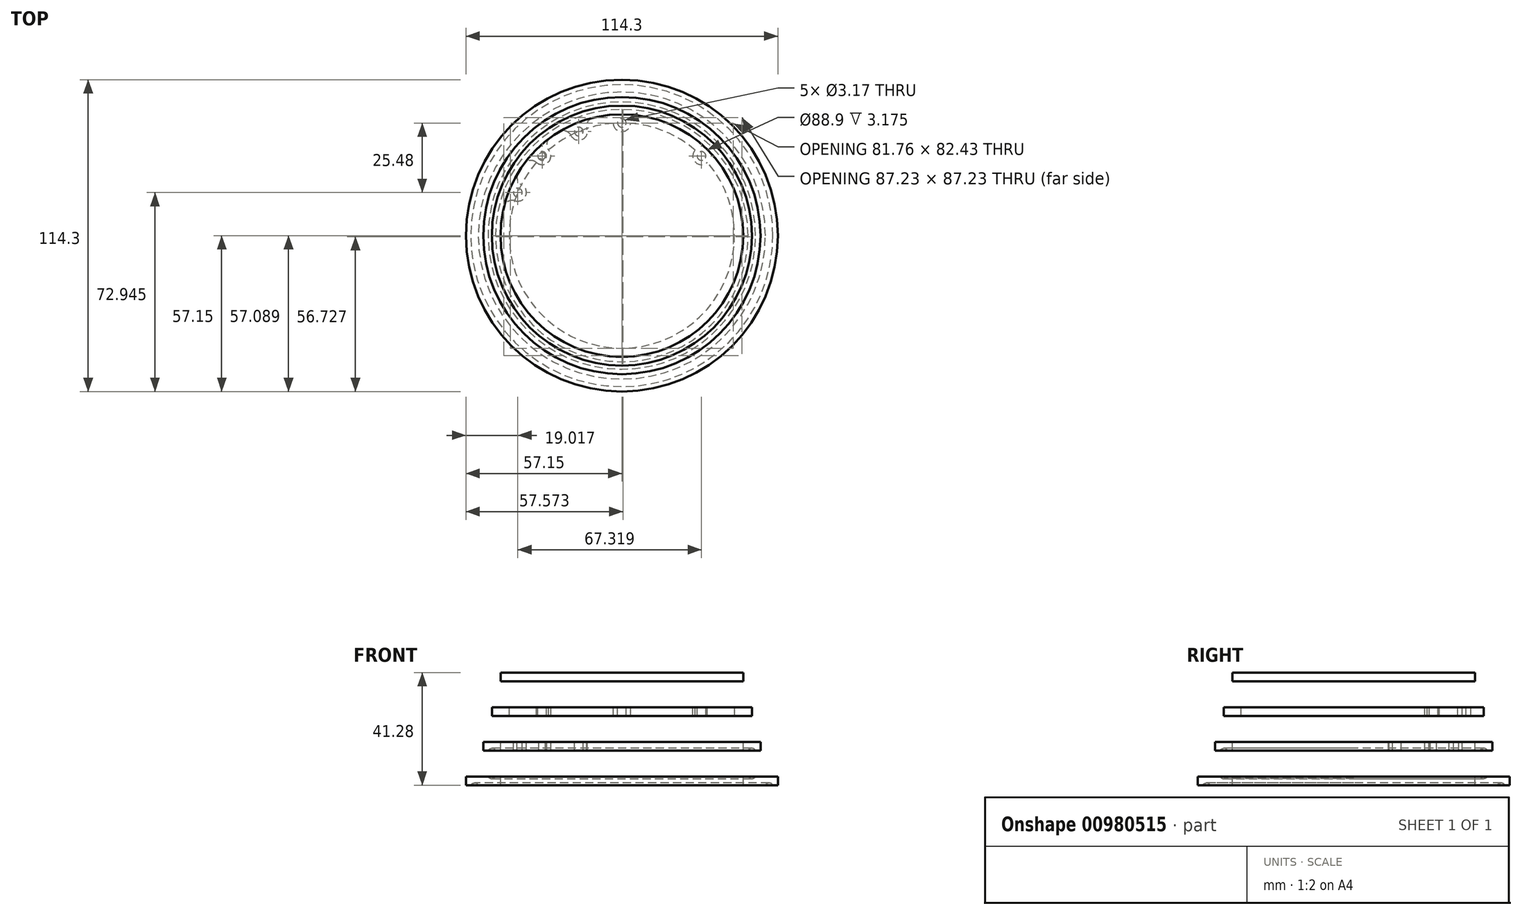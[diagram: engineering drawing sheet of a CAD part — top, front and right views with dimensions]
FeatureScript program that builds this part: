
annotation { "Feature Type Name" : "Feature", "Feature Type Description" : "" }
export const myFeature = defineFeature(function(context is Context, id is Id, definition is map)
    precondition{}
    {
        {
            var Q0;
            Q0=qCreatedBy(makeId("Front.planeOp"),FACE);
            var sketch = newSketch(context, id + "F0", { "sketchPlane" : qUnion([Q0])});
            skLineSegment(sketch, "E0.bottom", {"start": v(-44.45, 0) * mm, "end": v(-52.6, 0) * mm});
            skLineSegment(sketch, "E0.left", {"start": v(-44.45, 0) * mm, "end": v(-44.45, 3.17) * mm});
            skLineSegment(sketch, "E0.right", {"start": v(-57.15, 0) * mm, "end": v(-57.15, 3.17) * mm});
            skArc(sketch, "E1", {"start": v(-52.6, 0) * mm, "mid": v(-53.98, 0.8) * mm, "end": v(-55.35, 0) * mm});
            skArc(sketch, "E2", {"start": v(-49, 3.17) * mm, "mid": v(-47.62, 2.38) * mm, "end": v(-46.25, 3.17) * mm});
            skLineSegment(sketch, "E3", {"start": v(-57.15, 3.17) * mm, "end": v(-49, 3.17) * mm});
            skLineSegment(sketch, "E4", {"start": v(-49, 3.17) * mm, "end": v(-46.25, 3.17) * mm, "construction": true});
            skLineSegment(sketch, "E5", {"start": v(-46.25, 3.17) * mm, "end": v(-44.45, 3.17) * mm});
            skLineSegment(sketch, "E6", {"start": v(-55.35, 0) * mm, "end": v(-57.15, 0) * mm});
            skLineSegment(sketch, "E7", {"start": v(-52.6, 0) * mm, "end": v(-55.35, 0) * mm, "construction": true});
            skLineSegment(sketch, "E8", {"start": v(0, 3.17) * mm, "end": v(0, 0) * mm, "construction": true});
            skLineSegment(sketch, "E9.bottom", {"start": v(-44.45, 12.7) * mm, "end": v(-46.25, 12.7) * mm});
            skLineSegment(sketch, "E9.top", {"start": v(-44.45, 15.87) * mm, "end": v(-50.8, 15.87) * mm});
            skLineSegment(sketch, "E9.left", {"start": v(-44.45, 12.7) * mm, "end": v(-44.45, 15.87) * mm});
            skLineSegment(sketch, "E9.right", {"start": v(-50.8, 12.7) * mm, "end": v(-50.8, 15.87) * mm});
            skArc(sketch, "E10", {"start": v(-46.25, 12.7) * mm, "mid": v(-47.62, 13.5) * mm, "end": v(-49, 12.7) * mm});
            skLineSegment(sketch, "E11", {"start": v(-49, 12.7) * mm, "end": v(-50.8, 12.7) * mm});
            skLineSegment(sketch, "E12", {"start": v(-46.25, 12.7) * mm, "end": v(-49, 12.7) * mm, "construction": true});
            skLineSegment(sketch, "E13.bottom", {"start": v(-44.45, 41.27) * mm, "end": v(0, 41.27) * mm});
            skLineSegment(sketch, "E13.top", {"start": v(-44.45, 38.1) * mm, "end": v(0, 38.1) * mm});
            skLineSegment(sketch, "E13.left", {"start": v(-44.45, 41.27) * mm, "end": v(-44.45, 38.1) * mm});
            skLineSegment(sketch, "E13.right", {"start": v(0, 41.27) * mm, "end": v(0, 38.1) * mm});
            skLineSegment(sketch, "E14.bottom", {"start": v(-47.62, 28.57) * mm, "end": v(-41.27, 28.57) * mm});
            skLineSegment(sketch, "E14.top", {"start": v(-47.62, 25.4) * mm, "end": v(-41.27, 25.4) * mm});
            skLineSegment(sketch, "E14.left", {"start": v(-47.62, 28.57) * mm, "end": v(-47.62, 25.4) * mm});
            skLineSegment(sketch, "E14.right", {"start": v(-41.27, 28.57) * mm, "end": v(-41.27, 25.4) * mm});
            skSolve(sketch);
        }
        {
            var Q0;
            Q0=makeQuery(id+"F0.imprint","IMPRINT",FACE,{"disambiguationData":[TD([[makeQuery(id+"F0.imprint","IMPRINT",EDGE,{"derivedFrom":sQuery(id+"F0.wireOp",EDGE,"E0.bottom")}),-1.0]])]});
            var Q1;
            Q1=makeQuery(id+"F0.imprint","IMPRINT",FACE,{"disambiguationData":[TD([[makeQuery(id+"F0.imprint","IMPRINT",EDGE,{"derivedFrom":sQuery(id+"F0.wireOp",EDGE,"E9.bottom")}),-1.0]])]});
            var Q2;
            Q2=makeQuery(id+"F0.imprint","IMPRINT",FACE,{"disambiguationData":[TD([[makeQuery(id+"F0.imprint","IMPRINT",EDGE,{"derivedFrom":sQuery(id+"F0.wireOp",EDGE,"E13.bottom")}),-1.0]])]});
            var Q3;
            Q3=makeQuery(id+"F0.imprint","IMPRINT",FACE,{"disambiguationData":[TD([[makeQuery(id+"F0.imprint","IMPRINT",EDGE,{"derivedFrom":sQuery(id+"F0.wireOp",EDGE,"E14.bottom")}),-1.0]])]});
            var Q4;
            Q4=sQuery(id+"F0.wireOp",EDGE,"E8");
            revolve(context, id + "F1", {"surfaceOperationType" : NewSurfaceOperationType.NEW, "entities" : qUnion([Q0, Q1, Q2, Q3]), "axis" : qUnion([Q4]), "revolveType" : RevolveType.FULL});
        }
        {
            var Q0;
            Q0=qCreatedBy(makeId("Top.planeOp"),FACE);
            var sketch = newSketch(context, id + "F2", { "sketchPlane" : qUnion([Q0])});
            skCircle(sketch, "E15", {"center": v(0, 0) * mm, "radius": 44.45 * mm, "construction": true});
            skCircle(sketch, "E16", {"center": v(0, 0) * mm, "radius": 41.28 * mm, "construction": true});
            skPoint(sketch, "E17", {"position": v(-41.28, 0) * mm});
            skPoint(sketch, "E18.1.0", {"position": v(-38.13, -15.8) * mm});
            skPoint(sketch, "E18.2.0", {"position": v(-29.19, -29.19) * mm});
            skPoint(sketch, "E18.3.0", {"position": v(-15.8, -38.13) * mm});
            skPoint(sketch, "E18.4.0", {"position": v(0, -41.27) * mm});
            skPoint(sketch, "E18.5.0", {"position": v(15.8, -38.13) * mm});
            skPoint(sketch, "E18.6.0", {"position": v(29.19, -29.19) * mm});
            skPoint(sketch, "E18.7.0", {"position": v(38.13, -15.8) * mm});
            skPoint(sketch, "E18.8.0", {"position": v(41.27, 0) * mm});
            skPoint(sketch, "E18.9.0", {"position": v(38.13, 15.8) * mm});
            skPoint(sketch, "E18.10.0", {"position": v(29.19, 29.19) * mm});
            skPoint(sketch, "E18.11.0", {"position": v(15.8, 38.13) * mm});
            skPoint(sketch, "E19.0.12.0", {"position": v(0, 41.28) * mm});
            skPoint(sketch, "E19.0.13.0", {"position": v(-15.8, 38.13) * mm});
            skPoint(sketch, "E19.0.14.0", {"position": v(-29.19, 29.19) * mm});
            skPoint(sketch, "E19.0.15.0", {"position": v(-38.13, 15.8) * mm});
            skSolve(sketch);
        }
        {
            var Q0;
            Q0=makeQuery(id+"F1.opRevolve","SWEPT_FACE",FACE,{"disambiguationData":[OSD([sQuery(id+"F0.wireOp",EDGE,"E9.top")])]});
            var sketch = newSketch(context, id + "F3", { "sketchPlane" : qUnion([Q0])});
            skCircle(sketch, "E20", {"center": v(-38.13, 15.8) * mm, "radius": 1.59 * mm});
            skCircle(sketch, "E21", {"center": v(-15.8, 38.13) * mm, "radius": 1.59 * mm});
            skArc(sketch, "E22", {"start": v(-39.12, 12.78) * mm, "mid": v(-35.2, 14.58) * mm, "end": v(-36.7, 18.63) * mm});
            skArc(sketch, "E23", {"start": v(-18.63, 36.7) * mm, "mid": v(-14.58, 35.2) * mm, "end": v(-12.78, 39.12) * mm});
            skArc(sketch, "E24", {"start": v(-43.19, 10.5) * mm, "mid": v(31.43, -31.43) * mm, "end": v(-10.5, 43.19) * mm, "construction": true});
            skArc(sketch, "E25", {"start": v(-37.97, 23.1) * mm, "mid": v(-41.07, 17.01) * mm, "end": v(-43.19, 10.5) * mm});
            skArc(sketch, "E26", {"start": v(-23.1, 37.97) * mm, "mid": v(-31.43, 31.43) * mm, "end": v(-37.97, 23.1) * mm, "construction": true});
            skArc(sketch, "E27", {"start": v(-10.5, 43.19) * mm, "mid": v(-17.01, 41.07) * mm, "end": v(-23.1, 37.97) * mm});
            skPoint(sketch, "E28.visualSharp", {"position": v(-41.07, 17.01) * mm});
            skArc(sketch, "E28.filletArc", {"start": v(-39.12, 12.78) * mm, "mid": v(-41.65, 12.53) * mm, "end": v(-43.19, 10.5) * mm});
            skArc(sketch, "E29.filletArc", {"start": v(-37.97, 23.1) * mm, "mid": v(-38.31, 20.59) * mm, "end": v(-36.7, 18.63) * mm});
            skPoint(sketch, "E30.visualSharp", {"position": v(-17.01, 41.07) * mm});
            skArc(sketch, "E30.filletArc", {"start": v(-18.63, 36.7) * mm, "mid": v(-20.59, 38.31) * mm, "end": v(-23.1, 37.97) * mm});
            skArc(sketch, "E31.filletArc", {"start": v(-10.5, 43.19) * mm, "mid": v(-12.53, 41.65) * mm, "end": v(-12.78, 39.12) * mm});
            skCircle(sketch, "E32", {"center": v(-41.28, 0) * mm, "radius": 1.2 * mm});
            skCircle(sketch, "E33", {"center": v(-29.19, 29.19) * mm, "radius": 1.2 * mm});
            skArc(sketch, "E34", {"start": v(-41.03, -3.17) * mm, "mid": v(-38.1, 0) * mm, "end": v(-41.03, 3.17) * mm});
            skArc(sketch, "E35", {"start": v(-31.25, 26.77) * mm, "mid": v(-26.94, 26.94) * mm, "end": v(-26.77, 31.25) * mm});
            skArc(sketch, "E36", {"start": v(-43.92, 6.82) * mm, "mid": v(-43.28, 4.36) * mm, "end": v(-41.03, 3.17) * mm});
            skArc(sketch, "E37", {"start": v(-41.03, -3.17) * mm, "mid": v(-43.28, -4.36) * mm, "end": v(-43.92, -6.82) * mm});
            skArc(sketch, "E38", {"start": v(-31.25, 26.77) * mm, "mid": v(-33.68, 27.52) * mm, "end": v(-35.88, 26.24) * mm});
            skArc(sketch, "E39", {"start": v(-26.24, 35.88) * mm, "mid": v(-27.52, 33.68) * mm, "end": v(-26.77, 31.25) * mm});
            skSolve(sketch);
        }
        {
            var Q0;
            Q0=makeQuery(id+"F3.imprint","IMPRINT",FACE,{"disambiguationData":[TD([[makeQuery(id+"F3.imprint","IMPRINT",EDGE,{"derivedFrom":sQuery(id+"F3.wireOp",EDGE,"E20")}),-1.0]])]});
            var Q1;
            Q1=makeQuery(id+"F3.imprint","IMPRINT",FACE,{"disambiguationData":[TD([[makeQuery(id+"F3.imprint","IMPRINT",EDGE,{"derivedFrom":sQuery(id+"F3.wireOp",EDGE,"E21")}),-1.0]])]});
            var Q2;
            Q2=makeQuery(id+"F3.imprint","IMPRINT",FACE,{"disambiguationData":[TD([[makeQuery(id+"F3.imprint","IMPRINT",EDGE,{"derivedFrom":sQuery(id+"F3.wireOp",EDGE,"E33")}),-1.0]])]});
            var Q3;
            Q3=makeQuery(id+"F3.imprint","IMPRINT",FACE,{"disambiguationData":[TD([[makeQuery(id+"F3.imprint","IMPRINT",EDGE,{"derivedFrom":sQuery(id+"F3.wireOp",EDGE,"E32")}),-1.0]])]});
            var Q4;
            Q4=makeQuery(id+"F1.opRevolve","SWEPT_FACE",FACE,{"disambiguationData":[OSD([sQuery(id+"F0.wireOp",EDGE,"E9.bottom")])]});
            extrude(context, id + "F4", {"entities" : qUnion([Q0, Q1, Q2, Q3]), "operationType" : NewBodyOperationType.ADD, "endBound" : BoundingType.UP_TO_SURFACE, "oppositeDirection" : true, "depth" : 25.4 * mm, "endBoundEntityFace" : qUnion([Q4]), "offsetDistance" : 25.4 * mm});
        }
        {
            var Q0;
            {var subQ0=sQuery(id+"F3.wireOp",EDGE,"E39");var subQ1=sQuery(id+"F3.wireOp",EDGE,"E38");var subQ2=sQuery(id+"F3.wireOp",EDGE,"E35");var subQ3=sQuery(id+"F3.wireOp",EDGE,"E33");var subQ4=sQuery(id+"F0.wireOp",EDGE,"E9.left");var subQ5=sQuery(id+"F0.wireOp",EDGE,"E9.top");var subQ6=sQuery(id+"F3.wireOp",EDGE,"E37");var subQ7=sQuery(id+"F3.wireOp",EDGE,"E36");var subQ8=sQuery(id+"F3.wireOp",EDGE,"E34");var subQ9=sQuery(id+"F3.wireOp",EDGE,"E32");var subQ10=sQuery(id+"F3.wireOp",EDGE,"E31.filletArc");var subQ11=sQuery(id+"F3.wireOp",EDGE,"E30.filletArc");var subQ12=sQuery(id+"F3.wireOp",EDGE,"E27");var subQ13=sQuery(id+"F3.wireOp",EDGE,"E23");var subQ14=sQuery(id+"F3.wireOp",EDGE,"E21");var subQ15=sQuery(id+"F3.wireOp",EDGE,"E29.filletArc");var subQ16=sQuery(id+"F3.wireOp",EDGE,"E28.filletArc");var subQ17=sQuery(id+"F3.wireOp",EDGE,"E25");var subQ18=sQuery(id+"F3.wireOp",EDGE,"E22");var subQ19=sQuery(id+"F3.wireOp",EDGE,"E20");Q0=makeQuery(id+"FB8sXTdEjQkzu1t_4.3.F4.boolean.opBoolean","MERGE",FACE,{"derivedFrom":[makeQuery(id+"FB8sXTdEjQkzu1t_4.2.F4.boolean.opBoolean","MERGE",FACE,{"derivedFrom":[makeQuery(id+"FB8sXTdEjQkzu1t_4.1.F4.boolean.opBoolean","MERGE",FACE,{"derivedFrom":[makeQuery(id+"F4.boolean.opBoolean","MERGE",FACE,{"derivedFrom":[makeQuery(id+"F1.opRevolve","SWEPT_FACE",FACE,{"disambiguationData":[OSD([subQ5])]}),makeQuery(id+"F4.opExtrude","CAP_FACE",FACE,{"disambiguationData":[OSD([subQ19,subQ18,subQ17,subQ16,subQ15])],"isStart":true}),makeQuery(id+"F4.opExtrude","CAP_FACE",FACE,{"disambiguationData":[OSD([subQ14,subQ13,subQ12,subQ11,subQ10])],"isStart":true}),makeQuery(id+"F4.opExtrude","CAP_FACE",FACE,{"disambiguationData":[OSD([subQ5,subQ4,subQ9,subQ8,subQ7,subQ6])],"isStart":true}),makeQuery(id+"F4.opExtrude","CAP_FACE",FACE,{"disambiguationData":[OSD([subQ5,subQ4,subQ3,subQ2,subQ1,subQ0])],"isStart":true})]}),makeQuery(id+"FB8sXTdEjQkzu1t_4.1.F4.opExtrude","CAP_FACE",FACE,{"disambiguationData":[OSD([subQ19,subQ18,subQ17,subQ16,subQ15])],"isStart":true}),makeQuery(id+"FB8sXTdEjQkzu1t_4.1.F4.opExtrude","CAP_FACE",FACE,{"disambiguationData":[OSD([subQ14,subQ13,subQ12,subQ11,subQ10])],"isStart":true}),makeQuery(id+"FB8sXTdEjQkzu1t_4.1.F4.opExtrude","CAP_FACE",FACE,{"disambiguationData":[OSD([subQ5,subQ4,subQ9,subQ8,subQ7,subQ6])],"isStart":true}),makeQuery(id+"FB8sXTdEjQkzu1t_4.1.F4.opExtrude","CAP_FACE",FACE,{"disambiguationData":[OSD([subQ5,subQ4,subQ3,subQ2,subQ1,subQ0])],"isStart":true})]}),makeQuery(id+"FB8sXTdEjQkzu1t_4.2.F4.opExtrude","CAP_FACE",FACE,{"disambiguationData":[OSD([subQ19,subQ18,subQ17,subQ16,subQ15])],"isStart":true}),makeQuery(id+"FB8sXTdEjQkzu1t_4.2.F4.opExtrude","CAP_FACE",FACE,{"disambiguationData":[OSD([subQ14,subQ13,subQ12,subQ11,subQ10])],"isStart":true}),makeQuery(id+"FB8sXTdEjQkzu1t_4.2.F4.opExtrude","CAP_FACE",FACE,{"disambiguationData":[OSD([subQ5,subQ4,subQ9,subQ8,subQ7,subQ6])],"isStart":true}),makeQuery(id+"FB8sXTdEjQkzu1t_4.2.F4.opExtrude","CAP_FACE",FACE,{"disambiguationData":[OSD([subQ5,subQ4,subQ3,subQ2,subQ1,subQ0])],"isStart":true})]}),makeQuery(id+"FB8sXTdEjQkzu1t_4.3.F4.opExtrude","CAP_FACE",FACE,{"disambiguationData":[OSD([subQ19,subQ18,subQ17,subQ16,subQ15])],"isStart":true}),makeQuery(id+"FB8sXTdEjQkzu1t_4.3.F4.opExtrude","CAP_FACE",FACE,{"disambiguationData":[OSD([subQ14,subQ13,subQ12,subQ11,subQ10])],"isStart":true}),makeQuery(id+"FB8sXTdEjQkzu1t_4.3.F4.opExtrude","CAP_FACE",FACE,{"disambiguationData":[OSD([subQ5,subQ4,subQ9,subQ8,subQ7,subQ6])],"isStart":true}),makeQuery(id+"FB8sXTdEjQkzu1t_4.3.F4.opExtrude","CAP_FACE",FACE,{"disambiguationData":[OSD([subQ5,subQ4,subQ3,subQ2,subQ1,subQ0])],"isStart":true})]});}
            var sketch = newSketch(context, id + "F5", { "sketchPlane" : qUnion([Q0])});
            skArc(sketch, "E40", {"start": v(-43.19, 10.5) * mm, "mid": v(-44.45, 0) * mm, "end": v(-43.19, -10.5) * mm});
            skLineSegment(sketch, "E41", {"start": v(-43.19, 10.5) * mm, "end": v(43.19, 10.5) * mm});
            skLineSegment(sketch, "E42", {"start": v(43.19, -10.5) * mm, "end": v(-43.19, -10.5) * mm});
            skArc(sketch, "E43.trimOffspring", {"start": v(43.19, -10.5) * mm, "mid": v(44.45, 0) * mm, "end": v(43.19, 10.5) * mm});
            skSolve(sketch);
        }
        {
            var Q0;
            Q0=makeQuery(id+"F5.imprint","IMPRINT",FACE,{"disambiguationData":[TD([[makeQuery(id+"F5.imprint","IMPRINT",EDGE,{"derivedFrom":makeQuery(id+"F4.opExtrude","CAP_EDGE",EDGE,{"disambiguationData":[OSD([sQuery(id+"F3.wireOp",EDGE,"E32")])],"isStart":true})}),-1.0]])]});
            var Q1;
            Q1=makeQuery(id+"F5.imprint","IMPRINT",FACE,{"disambiguationData":[TD([[makeQuery(id+"F5.imprint","IMPRINT",EDGE,{"derivedFrom":makeQuery(id+"FB8sXTdEjQkzu1t_4.2.F4.opExtrude","CAP_EDGE",EDGE,{"disambiguationData":[OSD([sQuery(id+"F3.wireOp",EDGE,"E32")])],"isStart":true})}),-1.0]])]});
            extrude(context, id + "F6", {"entities" : qUnion([Q0, Q1]), "operationType" : NewBodyOperationType.REMOVE, "oppositeDirection" : true, "depth" : 25.4 * mm, "offsetDistance" : 25.4 * mm});
        }
        {
            var Q0;
            Q0=makeQuery(id+"F1.opRevolve","SWEPT_FACE",FACE,{"disambiguationData":[OSD([sQuery(id+"F0.wireOp",EDGE,"E14.bottom")])]});
            var sketch = newSketch(context, id + "F7", { "sketchPlane" : qUnion([Q0])});
            skCircle(sketch, "E44", {"center": v(-29.19, 29.19) * mm, "radius": 1.59 * mm});
            skCircle(sketch, "E45", {"center": v(-29.19, 29.19) * mm, "radius": 3.18 * mm});
            skCircle(sketch, "E46", {"center": v(0, 41.28) * mm, "radius": 3.18 * mm});
            skCircle(sketch, "E47", {"center": v(0, 41.28) * mm, "radius": 1.59 * mm});
            skCircle(sketch, "E48", {"center": v(29.19, 29.19) * mm, "radius": 3.18 * mm});
            skCircle(sketch, "E49", {"center": v(29.19, 29.19) * mm, "radius": 1.59 * mm});
            skSolve(sketch);
        }
        {
            var Q0;
            Q0 = qSketchRegion(id + "F7", true);
            var Q1;
            Q1=makeQuery(id+"F1.opRevolve","SWEPT_FACE",FACE,{"disambiguationData":[OSD([sQuery(id+"F0.wireOp",EDGE,"E14.top")])]});
            extrude(context, id + "F8", {"entities" : qUnion([Q0]), "operationType" : NewBodyOperationType.ADD, "endBound" : BoundingType.UP_TO_SURFACE, "oppositeDirection" : true, "depth" : 25.4 * mm, "endBoundEntityFace" : qUnion([Q1]), "offsetDistance" : 25.4 * mm});
        }
        {
            var Q0;
            {var subQ0=sQuery(id+"F7.wireOp",EDGE,"E44");var subQ1=makeQuery(id+"F1.opRevolve","SWEPT_EDGE",EDGE,{"disambiguationData":[OSD([sQuery(id+"F0.wireOp",EDGE,"E14.bottom"),sQuery(id+"F0.wireOp",EDGE,"E14.right")])]});var subQ2=makeQuery(id+"F7.imprint","INTERSECT",VERTEX,{"disambiguationData":[OD(0.0)],"derivedFrom":[subQ1,subQ0]});Q0=makeQuery(id+"F7.imprint","IMPRINT",FACE,{"disambiguationData":[TD([[makeQuery(id+"F7.imprint","IMPRINT",EDGE,{"disambiguationData":[TD([[subQ2,1.0]])],"derivedFrom":subQ0}),1.0]])]});}
            var Q1;
            {var subQ0=sQuery(id+"F7.wireOp",EDGE,"E47");var subQ1=makeQuery(id+"F1.opRevolve","SWEPT_EDGE",EDGE,{"disambiguationData":[OSD([sQuery(id+"F0.wireOp",EDGE,"E14.bottom"),sQuery(id+"F0.wireOp",EDGE,"E14.right")])]});var subQ2=makeQuery(id+"F7.imprint","INTERSECT",VERTEX,{"disambiguationData":[OD(0.0)],"derivedFrom":[subQ1,subQ0]});Q1=makeQuery(id+"F7.imprint","IMPRINT",FACE,{"disambiguationData":[TD([[makeQuery(id+"F7.imprint","IMPRINT",EDGE,{"disambiguationData":[TD([[subQ2,1.0]])],"derivedFrom":subQ0}),1.0]])]});}
            var Q2;
            {var subQ0=sQuery(id+"F7.wireOp",EDGE,"E49");var subQ1=makeQuery(id+"F1.opRevolve","SWEPT_EDGE",EDGE,{"disambiguationData":[OSD([sQuery(id+"F0.wireOp",EDGE,"E14.bottom"),sQuery(id+"F0.wireOp",EDGE,"E14.right")])]});var subQ2=makeQuery(id+"F7.imprint","INTERSECT",VERTEX,{"disambiguationData":[OD(0.0)],"derivedFrom":[subQ1,subQ0]});Q2=makeQuery(id+"F7.imprint","IMPRINT",FACE,{"disambiguationData":[TD([[makeQuery(id+"F7.imprint","IMPRINT",EDGE,{"disambiguationData":[TD([[subQ2,1.0]])],"derivedFrom":subQ0}),1.0]])]});}
            var Q3;
            Q3=makeQuery(id+"F8.boolean.opBoolean","MERGE",FACE,{"derivedFrom":[makeQuery(id+"F1.opRevolve","SWEPT_FACE",FACE,{"disambiguationData":[OSD([sQuery(id+"F0.wireOp",EDGE,"E14.top")])]}),makeQuery(id+"F8.opExtrude","CAP_FACE",FACE,{"disambiguationData":[OSD([sQuery(id+"F7.wireOp",EDGE,"E44"),sQuery(id+"F7.wireOp",EDGE,"E45")])],"isStart":false}),makeQuery(id+"F8.opExtrude","CAP_FACE",FACE,{"disambiguationData":[OSD([sQuery(id+"F7.wireOp",EDGE,"E46"),sQuery(id+"F7.wireOp",EDGE,"E47")])],"isStart":false}),makeQuery(id+"F8.opExtrude","CAP_FACE",FACE,{"disambiguationData":[OSD([sQuery(id+"F7.wireOp",EDGE,"E48"),sQuery(id+"F7.wireOp",EDGE,"E49")])],"isStart":false})]});
            extrude(context, id + "F9", {"entities" : qUnion([Q0, Q1, Q2]), "operationType" : NewBodyOperationType.REMOVE, "endBound" : BoundingType.UP_TO_SURFACE, "oppositeDirection" : true, "depth" : 25.4 * mm, "endBoundEntityFace" : qUnion([Q3]), "offsetDistance" : 25.4 * mm});
        }
    });
